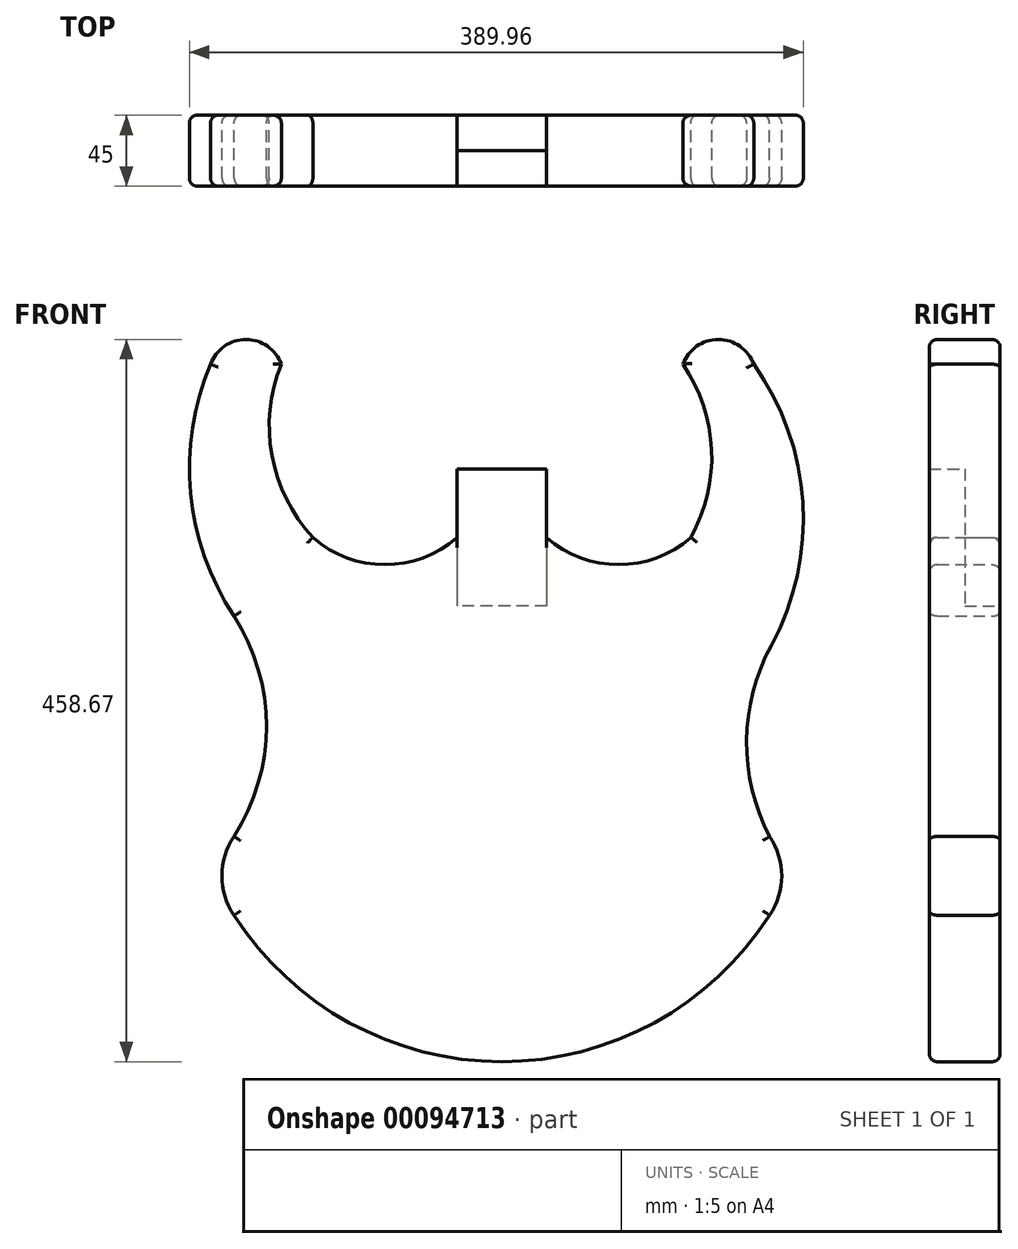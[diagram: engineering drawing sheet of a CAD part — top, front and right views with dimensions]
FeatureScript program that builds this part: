
annotation { "Feature Type Name" : "Feature", "Feature Type Description" : "" }
export const myFeature = defineFeature(function(context is Context, id is Id, definition is map)
    precondition{}
    {
        {
            var Q0;
            Q0=qCreatedBy(makeId("Front.planeOp"),FACE);
            var sketch = newSketch(context, id + "F0", { "sketchPlane" : qUnion([Q0])});
            skLineSegment(sketch, "E0.top", {"start": v(-120, -120) * mm, "end": v(120, -120) * mm});
            skLineSegment(sketch, "E0.left", {"start": v(-120, 120) * mm, "end": v(-120, -120) * mm});
            skLineSegment(sketch, "E0.right", {"start": v(120, 120) * mm, "end": v(120, -120) * mm});
            skPoint(sketch, "E0.middle", {"position": v(0, 0) * mm});
            skLineSegment(sketch, "E1", {"start": v(120, -120) * mm, "end": v(170, -120) * mm});
            skLineSegment(sketch, "E2", {"start": v(-120, -120) * mm, "end": v(-170, -120) * mm});
            skArc(sketch, "E3", {"start": v(-170, -120) * mm, "mid": v(0, -213.02) * mm, "end": v(170, -120) * mm});
            skLineSegment(sketch, "E4", {"start": v(170, -120) * mm, "end": v(170, -70) * mm});
            skLineSegment(sketch, "E5", {"start": v(-170, -120) * mm, "end": v(-170, -70) * mm});
            skArc(sketch, "E6", {"start": v(170, -120) * mm, "mid": v(177.8, -95) * mm, "end": v(170, -70) * mm});
            skArc(sketch, "E7", {"start": v(-170, -70) * mm, "mid": v(-177.8, -95) * mm, "end": v(-170, -120) * mm});
            skLineSegment(sketch, "E8", {"start": v(-170, 120) * mm, "end": v(-170, 70) * mm});
            skLineSegment(sketch, "E9", {"start": v(171.16, 101.39) * mm, "end": v(171.16, 51.39) * mm});
            skArc(sketch, "E10", {"start": v(-170, -70) * mm, "mid": v(-149.54, 0) * mm, "end": v(-170, 70) * mm});
            skArc(sketch, "E11", {"start": v(171.16, 51.39) * mm, "mid": v(155.54, -9.16) * mm, "end": v(170, -70) * mm});
            skLineSegment(sketch, "E12", {"start": v(-120, 120) * mm, "end": v(-145, 120) * mm});
            skLineSegment(sketch, "E13", {"start": v(120, 120) * mm, "end": v(145, 120) * mm});
            skLineSegment(sketch, "E14", {"start": v(145, 120) * mm, "end": v(145, 230) * mm});
            skLineSegment(sketch, "E15", {"start": v(-170, 120) * mm, "end": v(-170, 230) * mm});
            skLineSegment(sketch, "E16", {"start": v(-170, 230) * mm, "end": v(-185, 230) * mm});
            skLineSegment(sketch, "E17", {"start": v(145, 230) * mm, "end": v(160, 230) * mm});
            skLineSegment(sketch, "E18", {"start": v(-170, 230) * mm, "end": v(-140, 230) * mm});
            skLineSegment(sketch, "E19", {"start": v(145, 230) * mm, "end": v(115, 230) * mm});
            skArc(sketch, "E20", {"start": v(171.16, 51.39) * mm, "mid": v(191.16, 142.3) * mm, "end": v(160, 230) * mm});
            skArc(sketch, "E21", {"start": v(-185, 230) * mm, "mid": v(-197.73, 148.1) * mm, "end": v(-170, 70) * mm});
            skArc(sketch, "E22", {"start": v(-140, 230) * mm, "mid": v(-162.5, 245.65) * mm, "end": v(-185, 230) * mm});
            skArc(sketch, "E23", {"start": v(160, 230) * mm, "mid": v(137.5, 245.65) * mm, "end": v(115, 230) * mm});
            skArc(sketch, "E24", {"start": v(-140, 230) * mm, "mid": v(-146.04, 172.08) * mm, "end": v(-120, 120) * mm});
            skArc(sketch, "E25", {"start": v(120, 120) * mm, "mid": v(133.25, 175.72) * mm, "end": v(115, 230) * mm});
            skLineSegment(sketch, "E26.bottom", {"start": v(28.5, 163.5) * mm, "end": v(-28.5, 163.5) * mm});
            skLineSegment(sketch, "E26.top", {"start": v(28.5, 76.5) * mm, "end": v(-28.5, 76.5) * mm});
            skLineSegment(sketch, "E26.left", {"start": v(28.5, 163.5) * mm, "end": v(28.5, 76.5) * mm});
            skLineSegment(sketch, "E26.right", {"start": v(-28.5, 163.5) * mm, "end": v(-28.5, 76.5) * mm});
            skPoint(sketch, "E26.middle", {"position": v(0, 120) * mm});
            skArc(sketch, "E27", {"start": v(28.5, 120) * mm, "mid": v(74.25, 102.65) * mm, "end": v(120, 120) * mm});
            skArc(sketch, "E28", {"start": v(-120, 120) * mm, "mid": v(-74.25, 102.65) * mm, "end": v(-28.5, 120) * mm});
            skSolve(sketch);
        }
        {
            var Q0;
            Q0=makeQuery(id+"F0.imprint","IMPRINT",FACE,{"disambiguationData":[TD([[makeQuery(id+"F0.imprint","IMPRINT",EDGE,{"derivedFrom":sQuery(id+"F0.wireOp",EDGE,"E8")}),-1.0]])]});
            var Q1;
            Q1=makeQuery(id+"F0.imprint","IMPRINT",FACE,{"disambiguationData":[TD([[makeQuery(id+"F0.imprint","IMPRINT",EDGE,{"derivedFrom":sQuery(id+"F0.wireOp",EDGE,"E0.left")}),-1.0]])]});
            var Q2;
            Q2=makeQuery(id+"F0.imprint","IMPRINT",FACE,{"disambiguationData":[TD([[makeQuery(id+"F0.imprint","IMPRINT",EDGE,{"derivedFrom":sQuery(id+"F0.wireOp",EDGE,"E0.top")}),1.0]])]});
            var Q3;
            Q3=makeQuery(id+"F0.imprint","IMPRINT",FACE,{"disambiguationData":[TD([[makeQuery(id+"F0.imprint","IMPRINT",EDGE,{"derivedFrom":sQuery(id+"F0.wireOp",EDGE,"E16")}),-1.0]])]});
            var Q4;
            Q4=makeQuery(id+"F0.imprint","IMPRINT",FACE,{"disambiguationData":[TD([[makeQuery(id+"F0.imprint","IMPRINT",EDGE,{"derivedFrom":sQuery(id+"F0.wireOp",EDGE,"E0.top")}),-1.0]])]});
            var Q5;
            Q5=makeQuery(id+"F0.imprint","IMPRINT",FACE,{"disambiguationData":[TD([[makeQuery(id+"F0.imprint","IMPRINT",EDGE,{"derivedFrom":sQuery(id+"F0.wireOp",EDGE,"E0.right")}),1.0]])]});
            var Q6;
            Q6=makeQuery(id+"F0.imprint","IMPRINT",FACE,{"disambiguationData":[TD([[makeQuery(id+"F0.imprint","IMPRINT",EDGE,{"derivedFrom":sQuery(id+"F0.wireOp",EDGE,"E13")}),1.0]])]});
            var Q7;
            Q7=makeQuery(id+"F0.imprint","IMPRINT",FACE,{"disambiguationData":[TD([[makeQuery(id+"F0.imprint","IMPRINT",EDGE,{"derivedFrom":sQuery(id+"F0.wireOp",EDGE,"E17")}),1.0]])]});
            var Q8;
            Q8=makeQuery(id+"F0.imprint","IMPRINT",FACE,{"disambiguationData":[TD([[makeQuery(id+"F0.imprint","IMPRINT",EDGE,{"derivedFrom":sQuery(id+"F0.wireOp",EDGE,"E5")}),1.0]])]});
            var Q9;
            Q9=makeQuery(id+"F0.imprint","IMPRINT",FACE,{"disambiguationData":[TD([[makeQuery(id+"F0.imprint","IMPRINT",EDGE,{"derivedFrom":sQuery(id+"F0.wireOp",EDGE,"E4")}),-1.0]])]});
            extrude(context, id + "F1", {"entities" : qUnion([Q0, Q1, Q2, Q3, Q4, Q5, Q6, Q7, Q8, Q9]), "endBound" : BoundingType.SYMMETRIC, "depth" : 45 * mm});
        }
        {
            var Q0;
            {var subQ3=sQuery(id+"F0.wireOp",EDGE,"E26.bottom");Q0=makeQuery(id+"F0.imprint","IMPRINT",FACE,{"disambiguationData":[TD([[makeQuery(id+"F0.imprint","IMPRINT",EDGE,{"derivedFrom":subQ3}),1.0]])]});}
            extrude(context, id + "F2", {"entities" : qUnion([Q0]), "operationType" : NewBodyOperationType.ADD, "depth" : 22.5 * mm});
        }
        {
            var Q0;
            Q0=makeQuery(id+"F1.opExtrude","CAP_EDGE",EDGE,{"disambiguationData":[OSD([sQuery(id+"F0.wireOp",EDGE,"E28")])],"isStart":false});
            var Q1;
            Q1=makeQuery(id+"F1.opExtrude","CAP_EDGE",EDGE,{"disambiguationData":[OSD([sQuery(id+"F0.wireOp",EDGE,"E24")])],"isStart":false});
            var Q2;
            Q2=makeQuery(id+"F1.opExtrude","CAP_EDGE",EDGE,{"disambiguationData":[OSD([sQuery(id+"F0.wireOp",EDGE,"E22")])],"isStart":false});
            var Q3;
            Q3=makeQuery(id+"F1.opExtrude","CAP_EDGE",EDGE,{"disambiguationData":[OSD([sQuery(id+"F0.wireOp",EDGE,"E21")])],"isStart":false});
            var Q4;
            Q4=makeQuery(id+"F1.opExtrude","CAP_EDGE",EDGE,{"disambiguationData":[OSD([sQuery(id+"F0.wireOp",EDGE,"E10")])],"isStart":false});
            var Q5;
            Q5=makeQuery(id+"F1.opExtrude","CAP_EDGE",EDGE,{"disambiguationData":[OSD([sQuery(id+"F0.wireOp",EDGE,"E7")])],"isStart":false});
            var Q6;
            Q6=makeQuery(id+"F1.opExtrude","CAP_EDGE",EDGE,{"disambiguationData":[OSD([sQuery(id+"F0.wireOp",EDGE,"E3")])],"isStart":false});
            var Q7;
            Q7=makeQuery(id+"F1.opExtrude","CAP_EDGE",EDGE,{"disambiguationData":[OSD([sQuery(id+"F0.wireOp",EDGE,"E6")])],"isStart":false});
            var Q8;
            Q8=makeQuery(id+"F1.opExtrude","CAP_EDGE",EDGE,{"disambiguationData":[OSD([sQuery(id+"F0.wireOp",EDGE,"E11")])],"isStart":false});
            var Q9;
            Q9=makeQuery(id+"F1.opExtrude","CAP_EDGE",EDGE,{"disambiguationData":[OSD([sQuery(id+"F0.wireOp",EDGE,"E20")])],"isStart":false});
            var Q10;
            Q10=makeQuery(id+"F1.opExtrude","CAP_EDGE",EDGE,{"disambiguationData":[OSD([sQuery(id+"F0.wireOp",EDGE,"E23")])],"isStart":false});
            var Q11;
            Q11=makeQuery(id+"F1.opExtrude","CAP_EDGE",EDGE,{"disambiguationData":[OSD([sQuery(id+"F0.wireOp",EDGE,"E25")])],"isStart":false});
            var Q12;
            Q12=makeQuery(id+"F1.opExtrude","CAP_EDGE",EDGE,{"disambiguationData":[OSD([sQuery(id+"F0.wireOp",EDGE,"E27")])],"isStart":false});
            fillet(context, id + "F3", {"entities" : qUnion([Q0, Q1, Q2, Q3, Q4, Q5, Q6, Q7, Q8, Q9, Q10, Q11, Q12]), "radius" : 5 * mm, "tangentPropagation" : true, "allowEdgeOverflow" : false});
        }
        {
            var Q0;
            Q0=makeQuery(id+"F1.opExtrude","CAP_EDGE",EDGE,{"disambiguationData":[OSD([sQuery(id+"F0.wireOp",EDGE,"E23")])],"isStart":true});
            var Q1;
            Q1=makeQuery(id+"F1.opExtrude","CAP_EDGE",EDGE,{"disambiguationData":[OSD([sQuery(id+"F0.wireOp",EDGE,"E20")])],"isStart":true});
            var Q2;
            Q2=makeQuery(id+"F1.opExtrude","CAP_EDGE",EDGE,{"disambiguationData":[OSD([sQuery(id+"F0.wireOp",EDGE,"E11")])],"isStart":true});
            var Q3;
            Q3=makeQuery(id+"F1.opExtrude","CAP_EDGE",EDGE,{"disambiguationData":[OSD([sQuery(id+"F0.wireOp",EDGE,"E25")])],"isStart":true});
            var Q4;
            Q4=makeQuery(id+"F1.opExtrude","CAP_EDGE",EDGE,{"disambiguationData":[OSD([sQuery(id+"F0.wireOp",EDGE,"E27")])],"isStart":true});
            var Q5;
            Q5=makeQuery(id+"F1.opExtrude","CAP_EDGE",EDGE,{"disambiguationData":[OSD([sQuery(id+"F0.wireOp",EDGE,"E6")])],"isStart":true});
            var Q6;
            Q6=makeQuery(id+"F1.opExtrude","CAP_EDGE",EDGE,{"disambiguationData":[OSD([sQuery(id+"F0.wireOp",EDGE,"E3")])],"isStart":true});
            var Q7;
            Q7=makeQuery(id+"F1.opExtrude","CAP_EDGE",EDGE,{"disambiguationData":[OSD([sQuery(id+"F0.wireOp",EDGE,"E10")])],"isStart":true});
            var Q8;
            Q8=makeQuery(id+"F1.opExtrude","CAP_EDGE",EDGE,{"disambiguationData":[OSD([sQuery(id+"F0.wireOp",EDGE,"E7")])],"isStart":true});
            var Q9;
            Q9=makeQuery(id+"F1.opExtrude","CAP_EDGE",EDGE,{"disambiguationData":[OSD([sQuery(id+"F0.wireOp",EDGE,"E21")])],"isStart":true});
            var Q10;
            Q10=makeQuery(id+"F1.opExtrude","CAP_EDGE",EDGE,{"disambiguationData":[OSD([sQuery(id+"F0.wireOp",EDGE,"E24")])],"isStart":true});
            var Q11;
            Q11=makeQuery(id+"F1.opExtrude","CAP_EDGE",EDGE,{"disambiguationData":[OSD([sQuery(id+"F0.wireOp",EDGE,"E22")])],"isStart":true});
            var Q12;
            Q12=makeQuery(id+"F1.opExtrude","CAP_EDGE",EDGE,{"disambiguationData":[OSD([sQuery(id+"F0.wireOp",EDGE,"E28")])],"isStart":true});
            fillet(context, id + "F4", {"entities" : qUnion([Q0, Q1, Q2, Q3, Q4, Q5, Q6, Q7, Q8, Q9, Q10, Q11, Q12]), "radius" : 5 * mm, "tangentPropagation" : true, "allowEdgeOverflow" : false});
        }
    });
